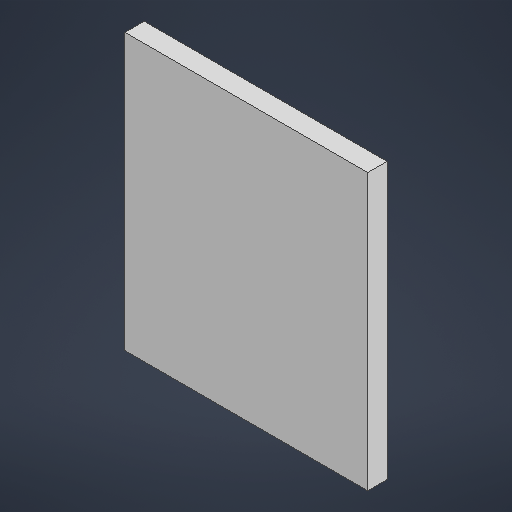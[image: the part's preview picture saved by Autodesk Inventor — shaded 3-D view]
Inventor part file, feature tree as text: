
AUTODESK INVENTOR PART (.ipt)
format: ipt  version: 2025 (Build 290162000, 162)  size: 189,440 bytes
history: native  units: mm
features: extrude x1, sketch x1
ambient origin geometry x8: Origin, YZ Plane, XZ Plane, XY Plane, X Axis, Y Axis, Z Axis, Center Point
bodies: 实体1 (feature_tree)
feature tree (2):
  extrude  "拉伸1"  Depth=71.5mm
  sketch  "草图1"  dims[d0=63.0mm d1=71.5mm d2=5.0mm d3=0.0mm]
